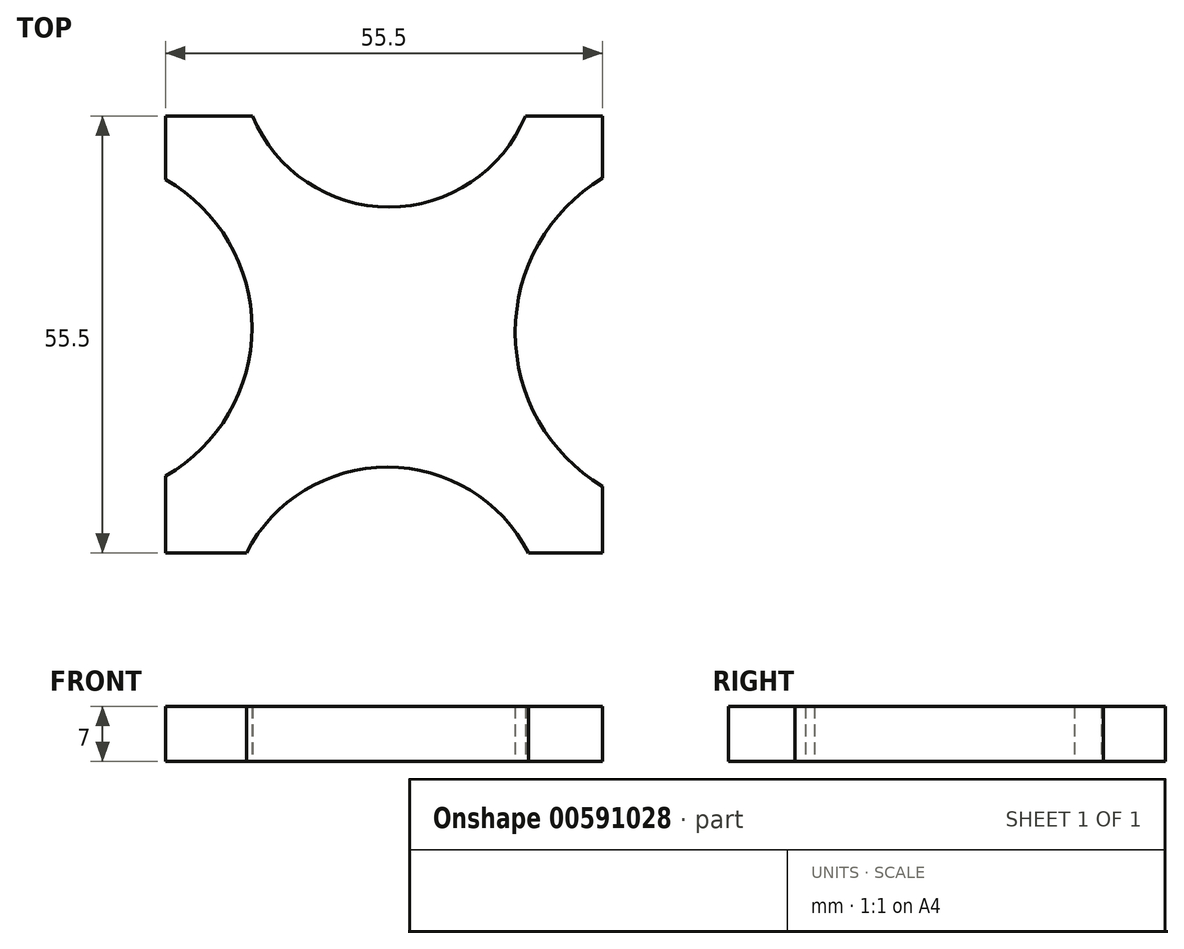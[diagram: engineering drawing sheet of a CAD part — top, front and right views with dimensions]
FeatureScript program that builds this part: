
annotation { "Feature Type Name" : "Feature", "Feature Type Description" : "" }
export const myFeature = defineFeature(function(context is Context, id is Id, definition is map)
    precondition{}
    {
        {
            var Q0;
            Q0=qCreatedBy(makeId("Top.planeOp"),FACE);
            var sketch = newSketch(context, id + "F0", { "sketchPlane" : qUnion([Q0])});
            skCircle(sketch, "E0", {"center": v(0, 0) * mm, "radius": 11.2 * mm});
            skLineSegment(sketch, "E1.bottom", {"start": v(-27.97, 28.3) * mm, "end": v(-16.93, 28.3) * mm});
            skLineSegment(sketch, "E1.top", {"start": v(-27.97, -27.2) * mm, "end": v(-17.71, -27.2) * mm});
            skLineSegment(sketch, "E1.left", {"start": v(-27.97, 28.3) * mm, "end": v(-27.97, 20.2) * mm});
            skLineSegment(sketch, "E1.right", {"start": v(27.53, 28.3) * mm, "end": v(27.53, 20.4) * mm});
            skArc(sketch, "E2", {"start": v(-16.93, 28.3) * mm, "mid": v(0.4, 16.74) * mm, "end": v(17.74, 28.3) * mm});
            skArc(sketch, "E3", {"start": v(-27.97, -17.4) * mm, "mid": v(-17, 1.4) * mm, "end": v(-27.97, 20.2) * mm});
            skArc(sketch, "E4", {"start": v(18.13, -27.2) * mm, "mid": v(0.2, -16.3) * mm, "end": v(-17.71, -27.2) * mm});
            skArc(sketch, "E5", {"start": v(27.53, 20.4) * mm, "mid": v(16.44, 0.8) * mm, "end": v(27.53, -18.78) * mm});
            skLineSegment(sketch, "E6.trimOffspring", {"start": v(17.74, 28.3) * mm, "end": v(27.53, 28.3) * mm});
            skLineSegment(sketch, "E7.trimOffspring", {"start": v(-27.97, -17.4) * mm, "end": v(-27.97, -27.2) * mm});
            skLineSegment(sketch, "E8.trimOffspring", {"start": v(18.13, -27.2) * mm, "end": v(27.53, -27.2) * mm});
            skLineSegment(sketch, "E9.trimOffspring", {"start": v(27.53, -18.78) * mm, "end": v(27.53, -27.2) * mm});
            skSolve(sketch);
        }
        {
            var Q0;
            Q0=makeQuery(id+"F0.imprint","IMPRINT",FACE,{"disambiguationData":[TD([[makeQuery(id+"F0.imprint","IMPRINT",EDGE,{"derivedFrom":sQuery(id+"F0.wireOp",EDGE,"E0")}),1.0]])]});
            var Q1;
            Q1=makeQuery(id+"F0.imprint","IMPRINT",FACE,{"disambiguationData":[TD([[makeQuery(id+"F0.imprint","IMPRINT",EDGE,{"derivedFrom":sQuery(id+"F0.wireOp",EDGE,"E0")}),-1.0]])]});
            extrude(context, id + "F1", {"entities" : qUnion([Q0, Q1]), "depth" : 7 * mm, "offsetDistance" : 25 * mm});
        }
    });
